# Revit family: Cutter_KE-5V_1_GENERADO
name_source: partatom
category: Equipos especializados
revit_build: Autodesk Revit 2016 (Build: 20151007_0715(x64)
units: mm (PartAtom-declared; Revit-internal decimal feet)

## family parameters
Compartido = No
Corte con vacíos al cargar = No
Cota de conector redondo = Diámetro de uso
Número OmniClass = 23.21.21.31.15
Punto de cálculo de habitación = No
Se basa en plano de trabajo = No
Siempre vertical = Sí
Tipo de pieza = Normal

## types (5) — shared parameters
Comentarios de tipo = Bowl capacity: 5.5 lt. Variable speed.
Depth = 387 mm  [stored 1.26969 ft]
Fabricante = SAMMIC S.L.
Foodservice Equipment Identifier = Sí
Height = 487 mm  [stored 1.59777 ft]
Phase = 1
Revision Code = 1
Specification by Manufacturer = To cut, grind, mix and knead any food in seconds.
Brushless technology: maximum efficiency.
URL = https://www.sammic.com
URL Cutsheet = http://www.sammic.com
Weight in Pounds = 39.7
Width = 286 mm  [stored 0.93832 ft]

## per-type parameters (varying)
| type | Conn Plug | Cycle | FL Amps | HP | Modelo | Volts | Watts |
| Cutter-Emulsifier KE-5V 230/50-60/1 | EU (SCHUKO 2P+G) | 50 Hz | 10 A | 2.01 | 1050834 | 230 V | 1500 W |
| Cutter-Emulsifier KE-5V 230/50-60/1 KSA | UK (BS 1363 13A / 2P+G) | 50 Hz | 10 A | 2.01 | 1050835 | 230 V | 1500 W |
| Cutter-Emulsifier KE-5V 120/50-60/1 | USA (NEMA 5-15P / 2P+G) | 60 Hz | 15 A |  | 1050836 | 120 V | 0 W |
| Cutter-Emulsifier KE-5V 230/50-60/1 AUS | AU/NZ (AS 3112 10A / 2P) | 50 Hz | 10 A | 2.01 | 1050838 | 230 V | 1500 W |
| Cutter-Emulsifier  KE-5V 230/50-60/1 K | EU (SCHUKO 2P+G) | 50 Hz | 10 A | 2.01 | 1050842 | 230 V | 1500 W |

note: column(s) folded — value = type name in every type: Descripción

note: [stored X ft] marks values corroborated as IEEE doubles in the binary element streams (Revit-internal decimal feet)

## geometry (parser evidence)
native form markers: Revolve x5
no freeform markers — native parametric forms only
